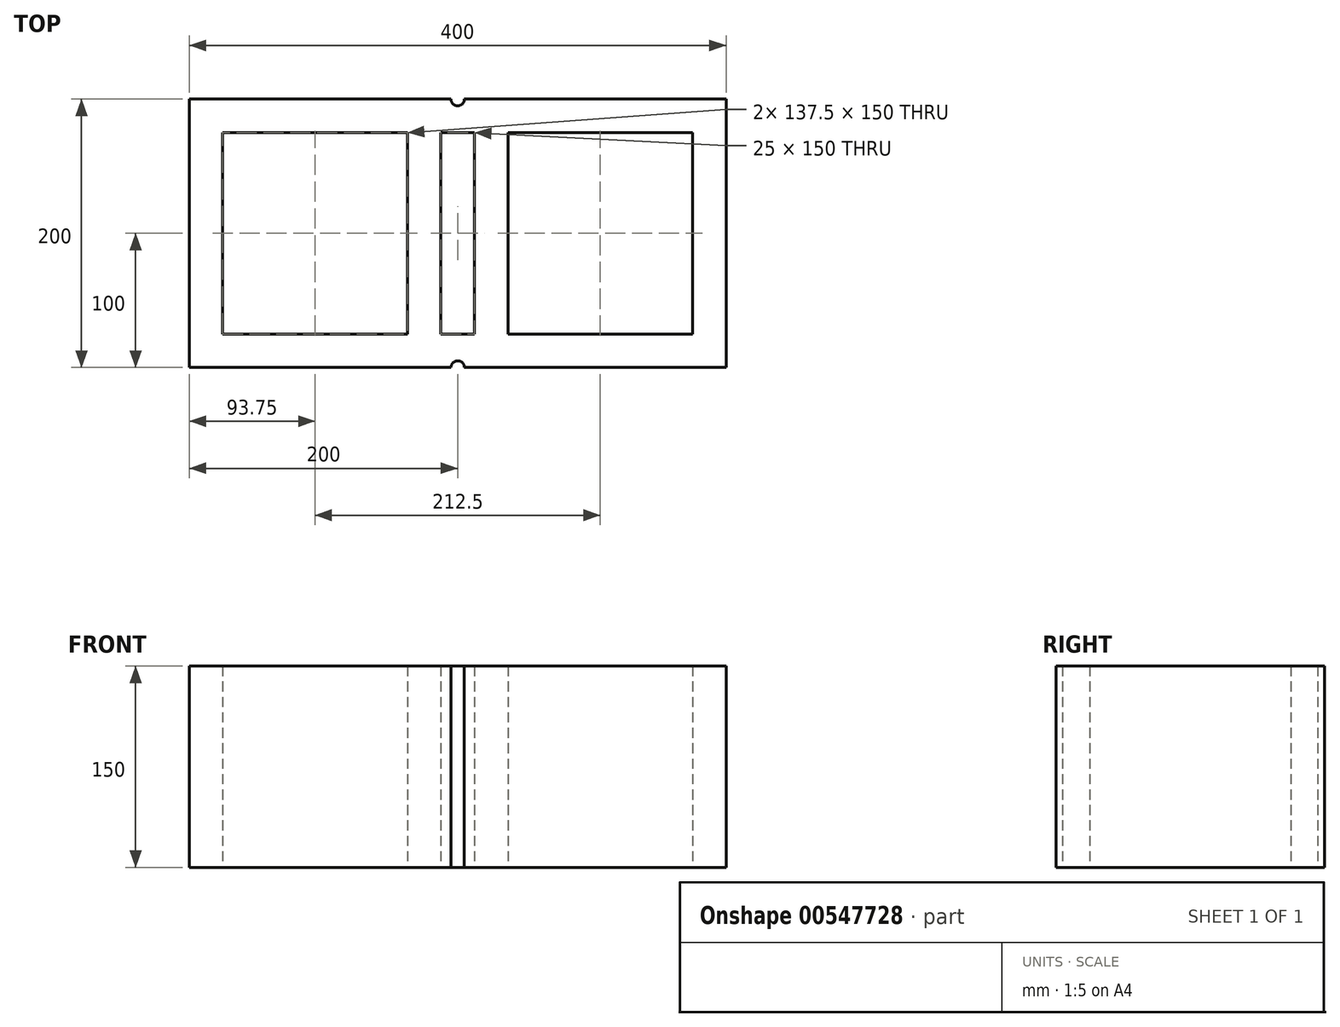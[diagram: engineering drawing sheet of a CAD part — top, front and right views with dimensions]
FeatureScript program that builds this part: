
annotation { "Feature Type Name" : "Feature", "Feature Type Description" : "" }
export const myFeature = defineFeature(function(context is Context, id is Id, definition is map)
    precondition{}
    {
        {
            var Q0;
            Q0=qCreatedBy(makeId("Top.planeOp"),FACE);
            var sketch = newSketch(context, id + "F0", { "sketchPlane" : qUnion([Q0])});
            skLineSegment(sketch, "E0.bottom", {"start": v(200, 100) * mm, "end": v(-200, 100) * mm});
            skLineSegment(sketch, "E0.top", {"start": v(200, -100) * mm, "end": v(-200, -100) * mm});
            skLineSegment(sketch, "E0.left", {"start": v(200, 100) * mm, "end": v(200, -100) * mm});
            skLineSegment(sketch, "E0.right", {"start": v(-200, 100) * mm, "end": v(-200, -100) * mm});
            skPoint(sketch, "E0.middle", {"position": v(0, 0) * mm});
            skLineSegment(sketch, "E1.bottom", {"start": v(-175, 75) * mm, "end": v(-37.5, 75) * mm});
            skLineSegment(sketch, "E1.top", {"start": v(-175, -75) * mm, "end": v(-37.5, -75) * mm});
            skLineSegment(sketch, "E1.left", {"start": v(-175, 75) * mm, "end": v(-175, -75) * mm});
            skLineSegment(sketch, "E1.right", {"start": v(-37.5, 75) * mm, "end": v(-37.5, -75) * mm});
            skLineSegment(sketch, "E2.bottom", {"start": v(37.5, 75) * mm, "end": v(175, 75) * mm});
            skLineSegment(sketch, "E2.top", {"start": v(37.5, -75) * mm, "end": v(175, -75) * mm});
            skLineSegment(sketch, "E2.left", {"start": v(37.5, 75) * mm, "end": v(37.5, -75) * mm});
            skLineSegment(sketch, "E2.right", {"start": v(175, 75) * mm, "end": v(175, -75) * mm});
            skLineSegment(sketch, "E3.bottom", {"start": v(-12.5, 75) * mm, "end": v(12.5, 75) * mm});
            skLineSegment(sketch, "E3.top", {"start": v(-12.5, -75) * mm, "end": v(12.5, -75) * mm});
            skLineSegment(sketch, "E3.left", {"start": v(-12.5, 75) * mm, "end": v(-12.5, -75) * mm});
            skLineSegment(sketch, "E3.right", {"start": v(12.5, 75) * mm, "end": v(12.5, -75) * mm});
            skArc(sketch, "E4", {"start": v(5, 100) * mm, "mid": v(0, 95) * mm, "end": v(-5, 100) * mm});
            skArc(sketch, "E5", {"start": v(-5, -100) * mm, "mid": v(0, -95) * mm, "end": v(5, -100) * mm});
            skSolve(sketch);
        }
        {
            var Q0;
            {var subQ1=sQuery(id+"F0.wireOp",EDGE,"E0.left");Q0=makeQuery(id+"F0.imprint","IMPRINT",FACE,{"disambiguationData":[TD([[makeQuery(id+"F0.imprint","IMPRINT",EDGE,{"derivedFrom":subQ1}),-1.0]])]});}
            extrude(context, id + "F1", {"entities" : qUnion([Q0]), "depth" : 150 * mm, "offsetDistance" : 25 * mm});
        }
    });
